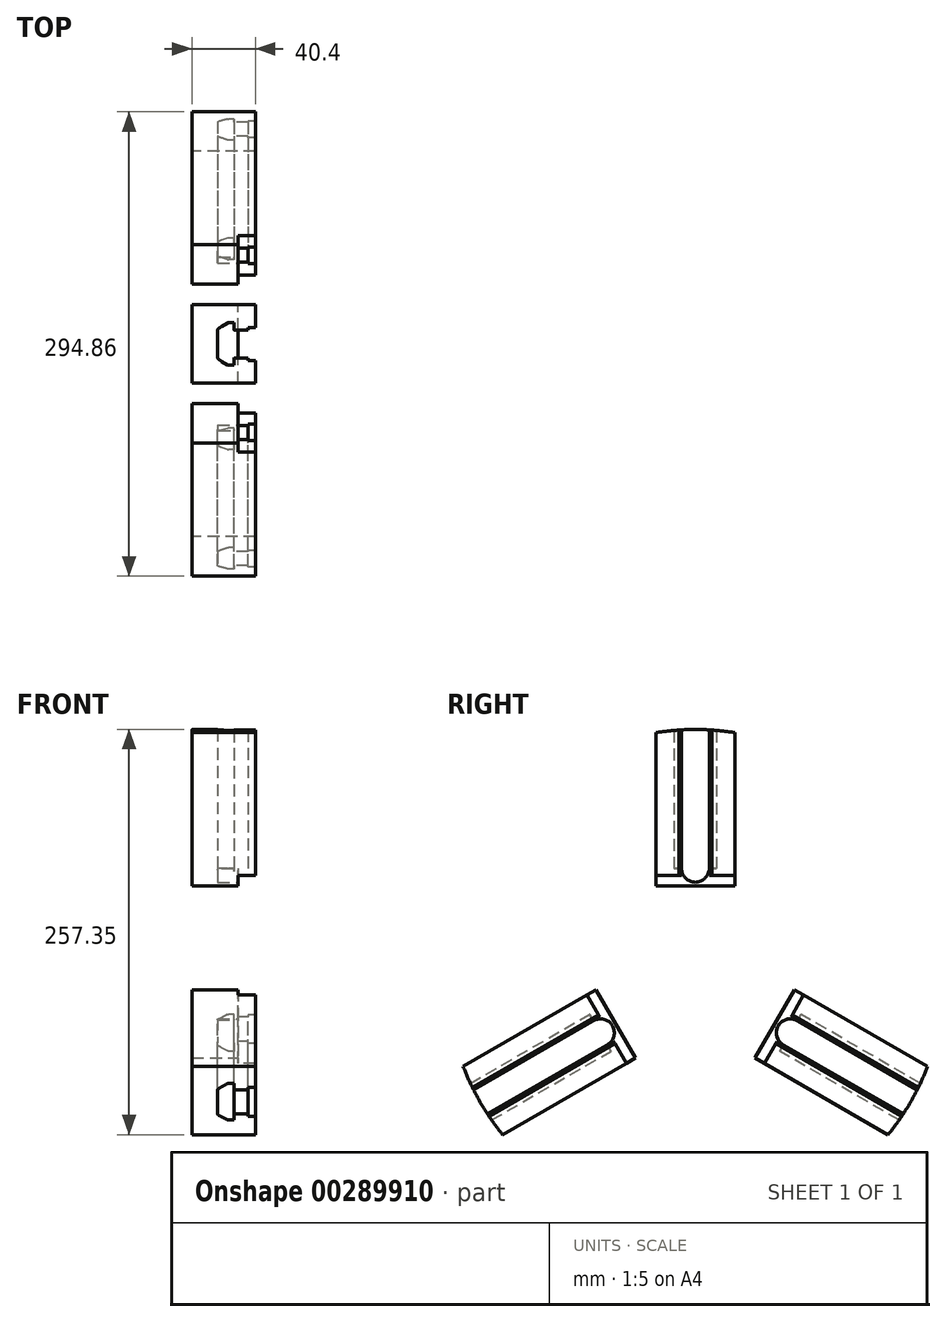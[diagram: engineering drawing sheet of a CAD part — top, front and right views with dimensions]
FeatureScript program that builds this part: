
annotation { "Feature Type Name" : "Feature", "Feature Type Description" : "" }
export const myFeature = defineFeature(function(context is Context, id is Id, definition is map)
    precondition{}
    {
        {
            var Q0;
            Q0=qCreatedBy(makeId("Right.planeOp"),FACE);
            var sketch = newSketch(context, id + "F0", { "sketchPlane" : qUnion([Q0])});
            skLineSegment(sketch, "E0", {"start": v(0, 65) * mm, "end": v(25, 65) * mm});
            skLineSegment(sketch, "E1", {"start": v(25, 65) * mm, "end": v(25, 155.8) * mm});
            skLineSegment(sketch, "E2", {"start": v(25, 155.8) * mm, "end": v(0, 155.8) * mm, "construction": true});
            skLineSegment(sketch, "E3", {"start": v(0, 155.8) * mm, "end": v(-25, 155.8) * mm, "construction": true});
            skLineSegment(sketch, "E4", {"start": v(-25, 155.8) * mm, "end": v(-25, 65) * mm});
            skLineSegment(sketch, "E5", {"start": v(-25, 65) * mm, "end": v(0, 65) * mm});
            skLineSegment(sketch, "E6", {"start": v(25, 65) * mm, "end": v(25, 58.3) * mm});
            skLineSegment(sketch, "E7", {"start": v(-25, 58.3) * mm, "end": v(-25, 65) * mm});
            skLineSegment(sketch, "E8", {"start": v(25, 58.3) * mm, "end": v(0, 58.3) * mm});
            skLineSegment(sketch, "E9", {"start": v(0, 58.3) * mm, "end": v(-25, 58.3) * mm});
            skArc(sketch, "E10", {"start": v(25, 155.8) * mm, "mid": v(0, 157.8) * mm, "end": v(-25, 155.8) * mm});
            skLineSegment(sketch, "E11.trimOffspring", {"start": v(0, 58.3) * mm, "end": v(0, 159.04) * mm, "construction": true});
            skPoint(sketch, "E12.start.orphan", {"position": v(0, 0) * mm});
            skLineSegment(sketch, "E13", {"start": v(0, 0) * mm, "end": v(0, 11) * mm, "construction": true});
            skLineSegment(sketch, "E14", {"start": v(0, 11) * mm, "end": v(0, 58.3) * mm, "construction": true});
            skSolve(sketch);
        }
        {
            var Q0;
            Q0=makeQuery(id+"F0.imprint","IMPRINT",FACE,{"disambiguationData":[TD([[makeQuery(id+"F0.imprint","IMPRINT",EDGE,{"derivedFrom":sQuery(id+"F0.wireOp",EDGE,"E0")}),1.0]])]});
            extrude(context, id + "F1", {"entities" : qUnion([Q0]), "depth" : 3 * mm, "hasSecondDirection" : true, "secondDirectionOppositeDirection" : true, "secondDirectionDepth" : 37.4 * mm});
        }
        {
            var Q0;
            Q0=makeQuery(id+"F0.imprint","IMPRINT",FACE,{"disambiguationData":[TD([[makeQuery(id+"F0.imprint","IMPRINT",EDGE,{"derivedFrom":sQuery(id+"F0.wireOp",EDGE,"E0")}),-1.0]])]});
            extrude(context, id + "F2", {"entities" : qUnion([Q0]), "operationType" : NewBodyOperationType.ADD, "oppositeDirection" : true, "depth" : 37.4 * mm, "hasSecondDirection" : true, "secondDirectionOppositeDirection" : true, "secondDirectionDepth" : 8 * mm});
        }
        {
            var Q0;
            Q0=makeQuery(id+"F1.opExtrude","SWEPT_FACE",FACE,{"disambiguationData":[OSD([sQuery(id+"F0.wireOp",EDGE,"E0"),sQuery(id+"F0.wireOp",EDGE,"E5")])]});
            var sketch = newSketch(context, id + "F3", { "sketchPlane" : qUnion([Q0])});
            skLineSegment(sketch, "E15", {"start": v(7.2, 0) * mm, "end": v(1.05, 0) * mm, "construction": true});
            skLineSegment(sketch, "E16", {"start": v(1.05, 0) * mm, "end": v(-20.37, 0) * mm, "construction": true});
            skLineSegment(sketch, "E17", {"start": v(3, 0) * mm, "end": v(3, 10.5) * mm});
            skLineSegment(sketch, "E18", {"start": v(3, 10.5) * mm, "end": v(-1.7, 10.5) * mm});
            skLineSegment(sketch, "E19", {"start": v(-1.7, 10.5) * mm, "end": v(-1.7, 8.85) * mm});
            skLineSegment(sketch, "E20", {"start": v(-1.7, 8.85) * mm, "end": v(-10.5, 8.85) * mm});
            skLineSegment(sketch, "E21", {"start": v(-10.5, 8.85) * mm, "end": v(-10.5, 13.5) * mm});
            skLineSegment(sketch, "E22", {"start": v(-10.5, 13.5) * mm, "end": v(-14.22, 13.5) * mm});
            skLineSegment(sketch, "E23", {"start": v(-14.74, 13.35) * mm, "end": v(-20.52, 9.8) * mm});
            skLineSegment(sketch, "E24", {"start": v(-21, 8.94) * mm, "end": v(-21, 0) * mm});
            skLineSegment(sketch, "E25.MirrorCS", {"start": v(3, 0) * mm, "end": v(3, -10.5) * mm});
            skLineSegment(sketch, "E26.MirrorCS", {"start": v(3, -10.5) * mm, "end": v(-1.7, -10.5) * mm});
            skLineSegment(sketch, "E27.MirrorCS", {"start": v(-1.7, -10.5) * mm, "end": v(-1.7, -8.85) * mm});
            skLineSegment(sketch, "E28.MirrorCS", {"start": v(-1.7, -8.85) * mm, "end": v(-10.5, -8.85) * mm});
            skLineSegment(sketch, "E29.MirrorCS", {"start": v(-10.5, -8.85) * mm, "end": v(-10.5, -13.5) * mm});
            skLineSegment(sketch, "E30.MirrorCS", {"start": v(-10.5, -13.5) * mm, "end": v(-14.22, -13.5) * mm});
            skLineSegment(sketch, "E31.MirrorCS", {"start": v(-14.74, -13.35) * mm, "end": v(-20.52, -9.8) * mm});
            skLineSegment(sketch, "E32.MirrorCS", {"start": v(-21, -8.94) * mm, "end": v(-21, 0) * mm});
            skPoint(sketch, "E33.visualSharp", {"position": v(-21, 9.5) * mm});
            skArc(sketch, "E33.filletArc", {"start": v(-20.52, 9.8) * mm, "mid": v(-20.87, 9.43) * mm, "end": v(-21, 8.94) * mm});
            skPoint(sketch, "E34.visualSharp", {"position": v(-21, -9.5) * mm});
            skArc(sketch, "E34.filletArc", {"start": v(-21, -8.94) * mm, "mid": v(-20.87, -9.43) * mm, "end": v(-20.52, -9.8) * mm});
            skPoint(sketch, "E35.visualSharp", {"position": v(-14.5, -13.5) * mm});
            skArc(sketch, "E35.filletArc", {"start": v(-14.74, -13.35) * mm, "mid": v(-14.49, -13.46) * mm, "end": v(-14.22, -13.5) * mm});
            skPoint(sketch, "E36.visualSharp", {"position": v(-14.5, 13.5) * mm});
            skArc(sketch, "E36.filletArc", {"start": v(-14.22, 13.5) * mm, "mid": v(-14.49, 13.46) * mm, "end": v(-14.74, 13.35) * mm});
            skPoint(sketch, "E37.visualSharp", {"position": v(-10.5, 13.5) * mm});
            skLineSegment(sketch, "E37.filletArc", {"start": v(-10.5, 13.5) * mm, "end": v(-10.5, 13.5) * mm});
            skPoint(sketch, "E38.visualSharp", {"position": v(-10.5, -13.5) * mm});
            skLineSegment(sketch, "E38.filletArc", {"start": v(-10.5, -13.5) * mm, "end": v(-10.5, -13.5) * mm});
            skLineSegment(sketch, "E39", {"start": v(-10.5, 8.85) * mm, "end": v(-10.5, -8.85) * mm});
            skSolve(sketch);
        }
        {
            var Q0;
            Q0=qSketchRegion(id+"F3",true);
            var Q1;
            Q1=makeQuery(id+"F1.opExtrude","SWEPT_FACE",FACE,{"disambiguationData":[OSD([sQuery(id+"F0.wireOp",EDGE,"E10")])]});
            extrude(context, id + "F4", {"entities" : qUnion([Q0]), "operationType" : NewBodyOperationType.REMOVE, "endBound" : BoundingType.UP_TO_SURFACE, "oppositeDirection" : true, "endBoundEntityFace" : qUnion([Q1]), "depth" : 25 * mm});
        }
        {
            var Q0;
            Q0=makeQuery(id+"F2.opExtrude","CAP_FACE",FACE,{"disambiguationData":[OSD([sQuery(id+"F0.wireOp",EDGE,"E0"),sQuery(id+"F0.wireOp",EDGE,"E5"),sQuery(id+"F0.wireOp",EDGE,"E6"),sQuery(id+"F0.wireOp",EDGE,"E7"),sQuery(id+"F0.wireOp",EDGE,"E8"),sQuery(id+"F0.wireOp",EDGE,"E9")])],"isStart":true});
            var sketch = newSketch(context, id + "F5", { "sketchPlane" : qUnion([Q0])});
            skArc(sketch, "E40", {"start": v(-8.85, 69.65) * mm, "mid": v(0, 60.8) * mm, "end": v(8.85, 69.65) * mm});
            skLineSegment(sketch, "E41", {"start": v(0, 157.8) * mm, "end": v(8.85, 157.8) * mm});
            skLineSegment(sketch, "E42", {"start": v(0, 157.8) * mm, "end": v(-8.85, 157.8) * mm});
            skLineSegment(sketch, "E43", {"start": v(-8.85, 157.8) * mm, "end": v(-8.85, 69.65) * mm});
            skLineSegment(sketch, "E44", {"start": v(8.85, 157.8) * mm, "end": v(8.85, 69.65) * mm});
            skSolve(sketch);
        }
        {
            var Q0;
            Q0=makeQuery(id+"F4.boolean.opBoolean","COPY",FACE,{"derivedFrom":makeQuery(id+"F4.opExtrude","CAP_FACE",FACE,{"disambiguationData":[OSD([sQuery(id+"F3.wireOp",EDGE,"E17"),sQuery(id+"F3.wireOp",EDGE,"E18"),sQuery(id+"F3.wireOp",EDGE,"E19"),sQuery(id+"F3.wireOp",EDGE,"E20"),sQuery(id+"F3.wireOp",EDGE,"E21"),sQuery(id+"F3.wireOp",EDGE,"E22"),sQuery(id+"F3.wireOp",EDGE,"E23"),sQuery(id+"F3.wireOp",EDGE,"E24"),sQuery(id+"F3.wireOp",EDGE,"E25.MirrorCS"),sQuery(id+"F3.wireOp",EDGE,"E26.MirrorCS"),sQuery(id+"F3.wireOp",EDGE,"E27.MirrorCS"),sQuery(id+"F3.wireOp",EDGE,"E28.MirrorCS"),sQuery(id+"F3.wireOp",EDGE,"E29.MirrorCS"),sQuery(id+"F3.wireOp",EDGE,"E30.MirrorCS"),sQuery(id+"F3.wireOp",EDGE,"E31.MirrorCS"),sQuery(id+"F3.wireOp",EDGE,"E32.MirrorCS"),sQuery(id+"F3.wireOp",EDGE,"E33.filletArc"),sQuery(id+"F3.wireOp",EDGE,"E34.filletArc"),sQuery(id+"F3.wireOp",EDGE,"E35.filletArc"),sQuery(id+"F3.wireOp",EDGE,"E36.filletArc")])],"isStart":true})});
            extrude(context, id + "F6", {"entities" : qUnion([Q0]), "operationType" : NewBodyOperationType.ADD, "depth" : 4.7 * mm});
        }
        {
            var Q0;
            {var subQ0=sQuery(id+"F5.wireOp",EDGE,"E40");var subQ1=sQuery(id+"F0.wireOp",EDGE,"E5");var subQ2=sQuery(id+"F0.wireOp",EDGE,"E0");var subQ3=makeQuery(id+"F4.boolean.opBoolean","SPLIT",EDGE,{"disambiguationData":[topologyDisambiguationEdgeConnected([makeQuery(id+"F2.opExtrude","CAP_FACE",FACE,{"disambiguationData":[OSD([subQ2,subQ1,sQuery(id+"F0.wireOp",EDGE,"E6"),sQuery(id+"F0.wireOp",EDGE,"E7"),sQuery(id+"F0.wireOp",EDGE,"E8"),sQuery(id+"F0.wireOp",EDGE,"E9")])],"isStart":true}),makeQuery(id+"F4.opExtrude","CAP_FACE",FACE,{"disambiguationData":[OSD([sQuery(id+"F3.wireOp",EDGE,"E17"),sQuery(id+"F3.wireOp",EDGE,"E18"),sQuery(id+"F3.wireOp",EDGE,"E19"),sQuery(id+"F3.wireOp",EDGE,"E20"),sQuery(id+"F3.wireOp",EDGE,"E21"),sQuery(id+"F3.wireOp",EDGE,"E22"),sQuery(id+"F3.wireOp",EDGE,"E23"),sQuery(id+"F3.wireOp",EDGE,"E24"),sQuery(id+"F3.wireOp",EDGE,"E25.MirrorCS"),sQuery(id+"F3.wireOp",EDGE,"E26.MirrorCS"),sQuery(id+"F3.wireOp",EDGE,"E27.MirrorCS"),sQuery(id+"F3.wireOp",EDGE,"E28.MirrorCS"),sQuery(id+"F3.wireOp",EDGE,"E29.MirrorCS"),sQuery(id+"F3.wireOp",EDGE,"E30.MirrorCS"),sQuery(id+"F3.wireOp",EDGE,"E31.MirrorCS"),sQuery(id+"F3.wireOp",EDGE,"E32.MirrorCS"),sQuery(id+"F3.wireOp",EDGE,"E33.filletArc"),sQuery(id+"F3.wireOp",EDGE,"E34.filletArc"),sQuery(id+"F3.wireOp",EDGE,"E35.filletArc"),sQuery(id+"F3.wireOp",EDGE,"E36.filletArc")])],"isStart":true})])],"derivedFrom":makeQuery(id+"F2.opExtrude","CAP_EDGE",EDGE,{"disambiguationData":[OSD([subQ2,subQ1])],"isStart":true})});var subQ4=makeQuery(id+"F5.imprint","INTERSECT",VERTEX,{"disambiguationData":[OD(0.0)],"derivedFrom":[subQ3,subQ0]});Q0=makeQuery(id+"F5.imprint","IMPRINT",FACE,{"disambiguationData":[TD([[makeQuery(id+"F5.imprint","IMPRINT",EDGE,{"disambiguationData":[TD([[subQ4,-1.0]])],"derivedFrom":subQ0}),1.0]])]});}
            var Q1;
            Q1=makeQuery(id+"F5.imprint","IMPRINT",FACE,{"disambiguationData":[TD([[makeQuery(id+"F5.imprint","IMPRINT",EDGE,{"derivedFrom":sQuery(id+"F5.wireOp",EDGE,"E41")}),-1.0]])]});
            var Q2;
            Q2=makeQuery(id+"F4.boolean.opBoolean","COPY",FACE,{"derivedFrom":makeQuery(id+"F4.opExtrude","SWEPT_FACE",FACE,{"disambiguationData":[OSD([sQuery(id+"F3.wireOp",EDGE,"E24"),sQuery(id+"F3.wireOp",EDGE,"E32.MirrorCS")])]})});
            extrude(context, id + "F7", {"entities" : qUnion([Q0, Q1]), "operationType" : NewBodyOperationType.REMOVE, "endBound" : BoundingType.UP_TO_SURFACE, "oppositeDirection" : true, "endBoundEntityFace" : qUnion([Q2]), "depth" : 25 * mm});
        }
        {
            var Q0;
            Q0=makeQuery(id+"F7.boolean.opBoolean","INTERSECT",EDGE,{"derivedFrom":[makeQuery(id+"F6.opExtrude","CAP_FACE",FACE,{"disambiguationData":[OSD([sQuery(id+"F3.wireOp",EDGE,"E17"),sQuery(id+"F3.wireOp",EDGE,"E18"),sQuery(id+"F3.wireOp",EDGE,"E19"),sQuery(id+"F3.wireOp",EDGE,"E20"),sQuery(id+"F3.wireOp",EDGE,"E21"),sQuery(id+"F3.wireOp",EDGE,"E22"),sQuery(id+"F3.wireOp",EDGE,"E23"),sQuery(id+"F3.wireOp",EDGE,"E24"),sQuery(id+"F3.wireOp",EDGE,"E25.MirrorCS"),sQuery(id+"F3.wireOp",EDGE,"E26.MirrorCS"),sQuery(id+"F3.wireOp",EDGE,"E27.MirrorCS"),sQuery(id+"F3.wireOp",EDGE,"E28.MirrorCS"),sQuery(id+"F3.wireOp",EDGE,"E29.MirrorCS"),sQuery(id+"F3.wireOp",EDGE,"E30.MirrorCS"),sQuery(id+"F3.wireOp",EDGE,"E31.MirrorCS"),sQuery(id+"F3.wireOp",EDGE,"E32.MirrorCS"),sQuery(id+"F3.wireOp",EDGE,"E33.filletArc"),sQuery(id+"F3.wireOp",EDGE,"E34.filletArc"),sQuery(id+"F3.wireOp",EDGE,"E35.filletArc"),sQuery(id+"F3.wireOp",EDGE,"E36.filletArc")])],"isStart":false}),makeQuery(id+"F7.opExtrude","SWEPT_FACE",FACE,{"disambiguationData":[OSD([sQuery(id+"F5.wireOp",EDGE,"E43")])]})]});
            var Q1;
            Q1=makeQuery(id+"F7.boolean.opBoolean","INTERSECT",EDGE,{"derivedFrom":[makeQuery(id+"F6.opExtrude","CAP_FACE",FACE,{"disambiguationData":[OSD([sQuery(id+"F3.wireOp",EDGE,"E17"),sQuery(id+"F3.wireOp",EDGE,"E18"),sQuery(id+"F3.wireOp",EDGE,"E19"),sQuery(id+"F3.wireOp",EDGE,"E20"),sQuery(id+"F3.wireOp",EDGE,"E21"),sQuery(id+"F3.wireOp",EDGE,"E22"),sQuery(id+"F3.wireOp",EDGE,"E23"),sQuery(id+"F3.wireOp",EDGE,"E24"),sQuery(id+"F3.wireOp",EDGE,"E25.MirrorCS"),sQuery(id+"F3.wireOp",EDGE,"E26.MirrorCS"),sQuery(id+"F3.wireOp",EDGE,"E27.MirrorCS"),sQuery(id+"F3.wireOp",EDGE,"E28.MirrorCS"),sQuery(id+"F3.wireOp",EDGE,"E29.MirrorCS"),sQuery(id+"F3.wireOp",EDGE,"E30.MirrorCS"),sQuery(id+"F3.wireOp",EDGE,"E31.MirrorCS"),sQuery(id+"F3.wireOp",EDGE,"E32.MirrorCS"),sQuery(id+"F3.wireOp",EDGE,"E33.filletArc"),sQuery(id+"F3.wireOp",EDGE,"E34.filletArc"),sQuery(id+"F3.wireOp",EDGE,"E35.filletArc"),sQuery(id+"F3.wireOp",EDGE,"E36.filletArc")])],"isStart":false}),makeQuery(id+"F7.opExtrude","SWEPT_FACE",FACE,{"disambiguationData":[OSD([sQuery(id+"F5.wireOp",EDGE,"E44")])]})]});
            fillet(context, id + "F8", {"entities" : qUnion([Q0, Q1]), "radius" : 2.5 * mm, "tangentPropagation" : true, "allowEdgeOverflow" : false});
        }
        {
            var Q0;
            Q0=qCreatedBy(makeId("Top.planeOp"),FACE);
            var sketch = newSketch(context, id + "F9", { "sketchPlane" : qUnion([Q0])});
            skLineSegment(sketch, "E45", {"start": v(0, 0) * mm, "end": v(3.6, 0) * mm, "construction": true});
            skSolve(sketch);
        }
        {
            var Q0;
            Q0=makeQuery(id+"F1.opExtrude","SWEPT_BODY",BODY,{"disambiguationData":[OSD([sQuery(id+"F0.wireOp",EDGE,"E0"),sQuery(id+"F0.wireOp",EDGE,"E1"),sQuery(id+"F0.wireOp",EDGE,"E4"),sQuery(id+"F0.wireOp",EDGE,"E5"),sQuery(id+"F0.wireOp",EDGE,"E10")])]});
            var Q1;
            Q1=sQuery(id+"F9.wireOp",EDGE,"E45");
            circularPattern(context, id + "F10", {"entities" : qUnion([Q0]), "axis" : qUnion([Q1]), "angle" : 360 * degree, "instanceCount" : 3, "equalSpace" : true});
        }
    });
